# Revit family: Reece_Accessory_Kado_Arc_Stool
name_source: partatom
category: Plumbing Fixtures
revit_build: Autodesk Revit 2018 (Build: 20190510_1515(x64)
units: mm (PartAtom-declared; Revit-internal decimal feet)

## family parameters
Cut with Voids When Loaded = Yes
Host = Face
Part Type = Normal
Room Calculation Point = Yes
Round Connector Dimension = Use Diameter
Shared = Yes

## types (1)
- American Solid Oak
    Default Elevation = 0 mm  [stored 0 ft]
    Description = Kado Arc Wooden Stool American Solid Oak
    Disclaimer = THIS FILE IS THE PROPERTY OF THE REECE GROUP. IT MAY NOT BE REPRODUCED, REVERSE-ENGINEERED OR MODIFIED. ANY REPUBLICATION, TRANSMISSION OR DISTRIBUTION FOR THE PURPOSE OF COMMERCIALLY EXPLOITING THE FILES IS PROHIBITED.
    Keynote = Product #9509653, Reece_Accessory_Kado_Arc_Stool - American Solid Oak
    Manufacturer = Kado
    Model = Arc
    Reece_Detail_Disclaimer = THIS FILE IS THE PROPERTY OF THE REECE GROUP. IT MAY NOT BE REPRODUCED, REVERSE-ENGINEERED OR MODIFIED. ANY REPUBLICATION, TRANSMISSION OR DISTRIBUTION FOR THE PURPOSE OF COMMERCIALLY EXPLOITING THE FILES IS PROHIBITED.
    Reece_Material_Main = Reece_Oak_American
    Reece_Overall_Depth = 367 mm  [stored 1.20407 ft]
    Reece_Overall_Height = 447 mm
    Reece_Overall_Width = 440 mm  [stored 1.44357 ft]
    Reece_Product_Brand = Kado
    Reece_Product_Description = Kado Arc Wooden Stool American Solid Oak
    Reece_Product_Mount = Floor Mounted
    Reece_Product_Number = 9509653
    Reece_Product_Sub Brand = Arc
    Reece_Product_Type = Accessory
    Reece_Product_Web Page = https://www.reece.com.au
    Type Comments = Accessory
    URL = https://www.reece.com.au

note: [stored X ft] marks values corroborated as IEEE doubles in the binary element streams (Revit-internal decimal feet)

## geometry (parser evidence)
native form markers: Sweep x2
no freeform markers — native parametric forms only
